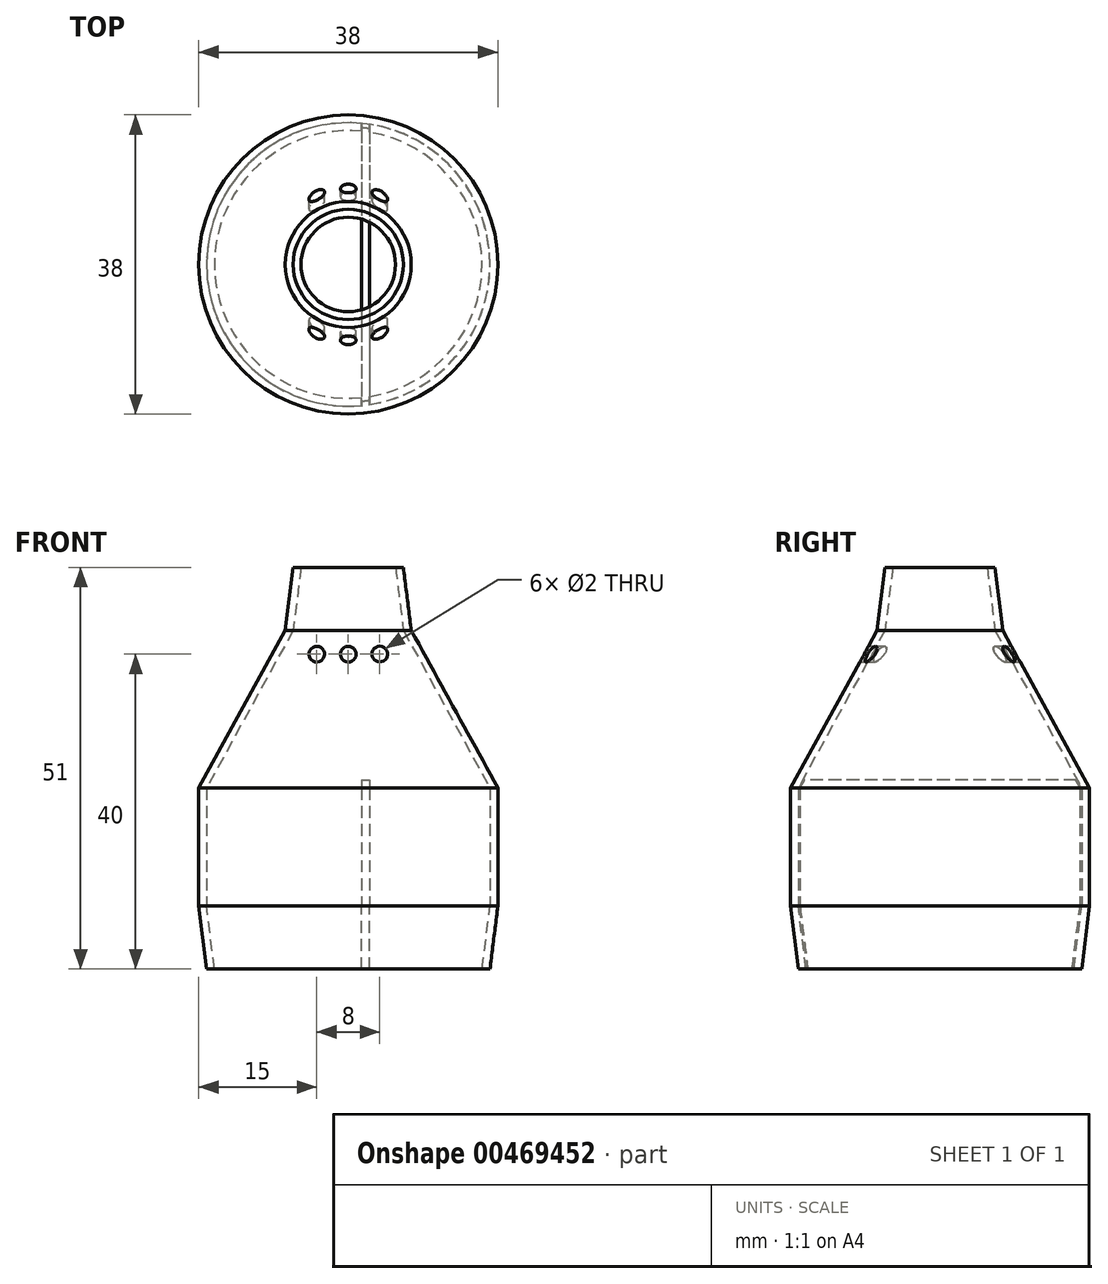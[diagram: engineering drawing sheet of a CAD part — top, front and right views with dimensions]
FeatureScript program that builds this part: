
annotation { "Feature Type Name" : "Feature", "Feature Type Description" : "" }
export const myFeature = defineFeature(function(context is Context, id is Id, definition is map)
    precondition{}
    {
        {
            var Q0;
            Q0=qCreatedBy(makeId("Top.planeOp"),FACE);
            var sketch = newSketch(context, id + "F0", { "sketchPlane" : qUnion([Q0])});
            skCircle(sketch, "E0", {"center": v(0, 0) * mm, "radius": 18 * mm});
            skCircle(sketch, "E1", {"center": v(0, 0) * mm, "radius": 19 * mm});
            skLineSegment(sketch, "E2", {"start": v(0, -19) * mm, "end": v(0, -18) * mm});
            skLineSegment(sketch, "E3.trimOffspring", {"start": v(0, 18) * mm, "end": v(0, 19) * mm});
            skPoint(sketch, "E4.center.orphan", {"position": v(-51.97, 0) * mm});
            skSolve(sketch);
        }
        {
            var Q0;
            {var subQ5=sQuery(id+"F0.wireOp",EDGE,"E2");Q0=makeQuery(id+"F0.imprint","IMPRINT",FACE,{"disambiguationData":[TD([[makeQuery(id+"F0.imprint","IMPRINT",EDGE,{"derivedFrom":subQ5}),-1.0]])]});}
            var Q1;
            {var subQ0=sQuery(id+"F0.wireOp",EDGE,"E2");Q1=makeQuery(id+"F0.imprint","IMPRINT",FACE,{"disambiguationData":[TD([[makeQuery(id+"F0.imprint","IMPRINT",EDGE,{"derivedFrom":subQ0}),1.0]])]});}
            extrude(context, id + "F1", {"entities" : qUnion([Q0, Q1]), "depth" : 15 * mm});
        }
        {
            var Q0;
            Q0=makeQuery(id+"F1.opExtrude","CAP_FACE",FACE,{"disambiguationData":[OSD([sQuery(id+"F0.wireOp",EDGE,"E0"),sQuery(id+"F0.wireOp",EDGE,"E1")])],"isStart":false});
            cPlane(context, id + "F2", {"entities" : qUnion([Q0]), "cplaneType" : CPlaneType.OFFSET, "offset" : 20 * mm, "width" : 150 * mm, "height" : 150 * mm});
        }
        {
            var Q0;
            Q0=makeQuery(id+"F1.opExtrude","CAP_FACE",FACE,{"disambiguationData":[OSD([sQuery(id+"F0.wireOp",EDGE,"E0"),sQuery(id+"F0.wireOp",EDGE,"E1")])],"isStart":false});
            var sketch = newSketch(context, id + "F3", { "sketchPlane" : qUnion([Q0])});
            skLineSegment(sketch, "E5", {"start": v(0, 19) * mm, "end": v(0, -19) * mm});
            skCircle(sketch, "E6", {"center": v(0, 0) * mm, "radius": 18 * mm});
            skCircle(sketch, "E7", {"center": v(0, 0) * mm, "radius": 19 * mm});
            skSolve(sketch);
        }
        {
            var Q0;
            Q0=qCreatedBy(id+"F2.planeOp",FACE);
            var sketch = newSketch(context, id + "F4", { "sketchPlane" : qUnion([Q0])});
            skCircle(sketch, "E8", {"center": v(0, 0) * mm, "radius": 7 * mm});
            skCircle(sketch, "E9", {"center": v(0, 0) * mm, "radius": 8 * mm});
            skLineSegment(sketch, "E10", {"start": v(0, 8) * mm, "end": v(0, 7) * mm});
            skLineSegment(sketch, "E11.trimOffspring", {"start": v(0, -7) * mm, "end": v(0, -8) * mm});
            skSolve(sketch);
        }
        {
            var Q1;
            {var subQ0=sQuery(id+"F3.wireOp",EDGE,"E7");var subQ1=sQuery(id+"F3.wireOp",EDGE,"E5");var subQ2=makeQuery(id+"F3.imprint","INTERSECT",VERTEX,{"disambiguationData":[OD(0.0)],"derivedFrom":[subQ1,subQ0]});var subQ3=sQuery(id+"F3.wireOp",EDGE,"E6");var subQ4=makeQuery(id+"F3.imprint","INTERSECT",VERTEX,{"disambiguationData":[OD(0.0)],"derivedFrom":[subQ1,subQ3]});Q1=makeQuery(id+"F3.imprint","IMPRINT",FACE,{"disambiguationData":[TD([[makeQuery(id+"F3.imprint","IMPRINT",EDGE,{"disambiguationData":[TD([[subQ2,-1.0],[subQ4,1.0]])],"derivedFrom":subQ1}),1.0]])]});}
            var Q2;
            {var subQ0=sQuery(id+"F4.wireOp",EDGE,"E10");Q2=makeQuery(id+"F4.imprint","IMPRINT",FACE,{"disambiguationData":[TD([[makeQuery(id+"F4.imprint","IMPRINT",EDGE,{"derivedFrom":subQ0}),1.0]])]});}
            loft(context, id + "F5", {"operationType" : NewBodyOperationType.ADD, "sheetProfilesArray" : [{ "sheetProfileEntities" : qUnion([Q1]) }, { "sheetProfileEntities" : qUnion([Q2]) }]});
        }
        {
            var Q1;
            {var subQ0=sQuery(id+"F3.wireOp",EDGE,"E7");var subQ1=sQuery(id+"F3.wireOp",EDGE,"E5");var subQ2=makeQuery(id+"F3.imprint","INTERSECT",VERTEX,{"disambiguationData":[OD(0.0)],"derivedFrom":[subQ1,subQ0]});var subQ3=sQuery(id+"F3.wireOp",EDGE,"E6");var subQ4=makeQuery(id+"F3.imprint","INTERSECT",VERTEX,{"disambiguationData":[OD(0.0)],"derivedFrom":[subQ1,subQ3]});Q1=makeQuery(id+"F3.imprint","IMPRINT",FACE,{"disambiguationData":[TD([[makeQuery(id+"F3.imprint","IMPRINT",EDGE,{"disambiguationData":[TD([[subQ2,-1.0],[subQ4,1.0]])],"derivedFrom":subQ1}),-1.0]])]});}
            var Q2;
            {var subQ0=sQuery(id+"F4.wireOp",EDGE,"E10");Q2=makeQuery(id+"F4.imprint","IMPRINT",FACE,{"disambiguationData":[TD([[makeQuery(id+"F4.imprint","IMPRINT",EDGE,{"derivedFrom":subQ0}),-1.0]])]});}
            loft(context, id + "F6", {"operationType" : NewBodyOperationType.ADD, "sheetProfilesArray" : [{ "sheetProfileEntities" : qUnion([Q1]) }, { "sheetProfileEntities" : qUnion([Q2]) }]});
        }
        {
            var Q0;
            Q0=qCreatedBy(makeId("Front.planeOp"),FACE);
            var sketch = newSketch(context, id + "F7", { "sketchPlane" : qUnion([Q0])});
            skCircle(sketch, "E12", {"center": v(0, 32) * mm, "radius": 1 * mm});
            skCircle(sketch, "E13", {"center": v(-4, 32) * mm, "radius": 1 * mm});
            skCircle(sketch, "E14", {"center": v(4, 32) * mm, "radius": 1 * mm});
            skLineSegment(sketch, "E15", {"start": v(-11.56, 32) * mm, "end": v(12.3, 32) * mm});
            skSolve(sketch);
        }
        {
            var Q0;
            {var subQ0=sQuery(id+"F7.wireOp",EDGE,"E15");var subQ1=sQuery(id+"F7.wireOp",EDGE,"E13");var subQ2=makeQuery(id+"F7.imprint","INTERSECT",VERTEX,{"disambiguationData":[OD(0.0)],"derivedFrom":[subQ1,subQ0]});Q0=makeQuery(id+"F7.imprint","IMPRINT",FACE,{"disambiguationData":[TD([[makeQuery(id+"F7.imprint","IMPRINT",EDGE,{"disambiguationData":[TD([[subQ2,-1.0]])],"derivedFrom":subQ1}),1.0]])]});}
            var Q1;
            {var subQ0=sQuery(id+"F7.wireOp",EDGE,"E15");var subQ1=sQuery(id+"F7.wireOp",EDGE,"E13");var subQ2=makeQuery(id+"F7.imprint","INTERSECT",VERTEX,{"disambiguationData":[OD(0.0)],"derivedFrom":[subQ1,subQ0]});Q1=makeQuery(id+"F7.imprint","IMPRINT",FACE,{"disambiguationData":[TD([[makeQuery(id+"F7.imprint","IMPRINT",EDGE,{"disambiguationData":[TD([[subQ2,1.0]])],"derivedFrom":subQ1}),1.0]])]});}
            var Q2;
            {var subQ0=sQuery(id+"F7.wireOp",EDGE,"E15");var subQ1=sQuery(id+"F7.wireOp",EDGE,"E12");var subQ2=makeQuery(id+"F7.imprint","INTERSECT",VERTEX,{"disambiguationData":[OD(0.0)],"derivedFrom":[subQ1,subQ0]});Q2=makeQuery(id+"F7.imprint","IMPRINT",FACE,{"disambiguationData":[TD([[makeQuery(id+"F7.imprint","IMPRINT",EDGE,{"disambiguationData":[TD([[subQ2,1.0]])],"derivedFrom":subQ1}),1.0]])]});}
            var Q3;
            {var subQ0=sQuery(id+"F7.wireOp",EDGE,"E15");var subQ1=sQuery(id+"F7.wireOp",EDGE,"E12");var subQ2=makeQuery(id+"F7.imprint","INTERSECT",VERTEX,{"disambiguationData":[OD(0.0)],"derivedFrom":[subQ1,subQ0]});Q3=makeQuery(id+"F7.imprint","IMPRINT",FACE,{"disambiguationData":[TD([[makeQuery(id+"F7.imprint","IMPRINT",EDGE,{"disambiguationData":[TD([[subQ2,-1.0]])],"derivedFrom":subQ1}),1.0]])]});}
            var Q4;
            {var subQ0=sQuery(id+"F7.wireOp",EDGE,"E15");var subQ1=sQuery(id+"F7.wireOp",EDGE,"E14");var subQ2=makeQuery(id+"F7.imprint","INTERSECT",VERTEX,{"disambiguationData":[OD(0.0)],"derivedFrom":[subQ1,subQ0]});Q4=makeQuery(id+"F7.imprint","IMPRINT",FACE,{"disambiguationData":[TD([[makeQuery(id+"F7.imprint","IMPRINT",EDGE,{"disambiguationData":[TD([[subQ2,1.0]])],"derivedFrom":subQ1}),1.0]])]});}
            var Q5;
            {var subQ0=sQuery(id+"F7.wireOp",EDGE,"E15");var subQ1=sQuery(id+"F7.wireOp",EDGE,"E14");var subQ2=makeQuery(id+"F7.imprint","INTERSECT",VERTEX,{"disambiguationData":[OD(0.0)],"derivedFrom":[subQ1,subQ0]});Q5=makeQuery(id+"F7.imprint","IMPRINT",FACE,{"disambiguationData":[TD([[makeQuery(id+"F7.imprint","IMPRINT",EDGE,{"disambiguationData":[TD([[subQ2,-1.0]])],"derivedFrom":subQ1}),1.0]])]});}
            extrude(context, id + "F8", {"entities" : qUnion([Q0, Q1, Q2, Q3, Q4, Q5]), "operationType" : NewBodyOperationType.REMOVE, "depth" : 12 * mm, "hasSecondDirection" : true, "secondDirectionOppositeDirection" : true, "secondDirectionDepth" : 12 * mm});
        }
        {
            var Q0;
            {var subQ0=sQuery(id+"F4.wireOp",EDGE,"E10");Q0=makeQuery(id+"F4.imprint","IMPRINT",FACE,{"disambiguationData":[TD([[makeQuery(id+"F4.imprint","IMPRINT",EDGE,{"derivedFrom":subQ0}),1.0]])]});}
            cPlane(context, id + "F9", {"entities" : qUnion([Q0]), "cplaneType" : CPlaneType.OFFSET, "offset" : 8 * mm, "width" : 150 * mm, "height" : 150 * mm});
        }
        {
            var Q0;
            Q0=qCreatedBy(id+"F9.planeOp",FACE);
            var sketch = newSketch(context, id + "F10", { "sketchPlane" : qUnion([Q0])});
            skCircle(sketch, "E16", {"center": v(0, 0) * mm, "radius": 7 * mm});
            skCircle(sketch, "E17", {"center": v(0, 0) * mm, "radius": 6 * mm});
            skLineSegment(sketch, "E18", {"start": v(0, 7) * mm, "end": v(0, 6) * mm});
            skLineSegment(sketch, "E19.trimOffspring", {"start": v(0, -6) * mm, "end": v(0, -7) * mm});
            skSolve(sketch);
        }
        {
            var Q1;
            {var subQ0=sQuery(id+"F4.wireOp",EDGE,"E10");Q1=makeQuery(id+"F4.imprint","IMPRINT",FACE,{"disambiguationData":[TD([[makeQuery(id+"F4.imprint","IMPRINT",EDGE,{"derivedFrom":subQ0}),-1.0]])]});}
            var Q2;
            {var subQ0=sQuery(id+"F10.wireOp",EDGE,"E18");Q2=makeQuery(id+"F10.imprint","IMPRINT",FACE,{"disambiguationData":[TD([[makeQuery(id+"F10.imprint","IMPRINT",EDGE,{"derivedFrom":subQ0}),-1.0]])]});}
            loft(context, id + "F11", {"operationType" : NewBodyOperationType.ADD, "sheetProfilesArray" : [{ "sheetProfileEntities" : qUnion([Q1]) }, { "sheetProfileEntities" : qUnion([Q2]) }]});
        }
        {
            var Q1;
            {var subQ0=sQuery(id+"F4.wireOp",EDGE,"E10");Q1=makeQuery(id+"F4.imprint","IMPRINT",FACE,{"disambiguationData":[TD([[makeQuery(id+"F4.imprint","IMPRINT",EDGE,{"derivedFrom":subQ0}),1.0]])]});}
            var Q2;
            {var subQ0=sQuery(id+"F10.wireOp",EDGE,"E18");Q2=makeQuery(id+"F10.imprint","IMPRINT",FACE,{"disambiguationData":[TD([[makeQuery(id+"F10.imprint","IMPRINT",EDGE,{"derivedFrom":subQ0}),1.0]])]});}
            loft(context, id + "F12", {"operationType" : NewBodyOperationType.ADD, "sheetProfilesArray" : [{ "sheetProfileEntities" : qUnion([Q1]) }, { "sheetProfileEntities" : qUnion([Q2]) }]});
        }
        {
            var Q0;
            Q0=qCreatedBy(makeId("Top.planeOp"),FACE);
            cPlane(context, id + "F13", {"entities" : qUnion([Q0]), "cplaneType" : CPlaneType.OFFSET, "offset" : 8 * mm, "oppositeDirection" : true, "width" : 150 * mm, "height" : 150 * mm});
        }
        {
            var Q0;
            Q0=qCreatedBy(id+"F13.planeOp",FACE);
            var sketch = newSketch(context, id + "F14", { "sketchPlane" : qUnion([Q0])});
            skCircle(sketch, "E20", {"center": v(0, 0) * mm, "radius": 17 * mm});
            skCircle(sketch, "E21", {"center": v(0, 0) * mm, "radius": 18 * mm});
            skLineSegment(sketch, "E22", {"start": v(0, -18) * mm, "end": v(0, 18) * mm});
            skSolve(sketch);
        }
        {
            var Q1;
            {var subQ0=sQuery(id+"F0.wireOp",EDGE,"E2");Q1=makeQuery(id+"F0.imprint","IMPRINT",FACE,{"disambiguationData":[TD([[makeQuery(id+"F0.imprint","IMPRINT",EDGE,{"derivedFrom":subQ0}),1.0]])]});}
            var Q2;
            {var subQ0=sQuery(id+"F14.wireOp",EDGE,"E22");var subQ1=sQuery(id+"F14.wireOp",EDGE,"E20");var subQ2=makeQuery(id+"F14.imprint","INTERSECT",VERTEX,{"disambiguationData":[OD(0.0)],"derivedFrom":[subQ1,subQ0]});Q2=makeQuery(id+"F14.imprint","IMPRINT",FACE,{"disambiguationData":[TD([[makeQuery(id+"F14.imprint","IMPRINT",EDGE,{"disambiguationData":[TD([[subQ2,1.0]])],"derivedFrom":subQ1}),-1.0]])]});}
            loft(context, id + "F15", {"operationType" : NewBodyOperationType.ADD, "sheetProfilesArray" : [{ "sheetProfileEntities" : qUnion([Q1]) }, { "sheetProfileEntities" : qUnion([Q2]) }]});
        }
        {
            var Q1;
            {var subQ0=sQuery(id+"F14.wireOp",EDGE,"E22");var subQ1=sQuery(id+"F14.wireOp",EDGE,"E20");var subQ2=makeQuery(id+"F14.imprint","INTERSECT",VERTEX,{"disambiguationData":[OD(0.0)],"derivedFrom":[subQ1,subQ0]});Q1=makeQuery(id+"F14.imprint","IMPRINT",FACE,{"disambiguationData":[TD([[makeQuery(id+"F14.imprint","IMPRINT",EDGE,{"disambiguationData":[TD([[subQ2,-1.0]])],"derivedFrom":subQ1}),-1.0]])]});}
            var Q2;
            {var subQ5=sQuery(id+"F0.wireOp",EDGE,"E2");Q2=makeQuery(id+"F0.imprint","IMPRINT",FACE,{"disambiguationData":[TD([[makeQuery(id+"F0.imprint","IMPRINT",EDGE,{"derivedFrom":subQ5}),-1.0]])]});}
            loft(context, id + "F16", {"operationType" : NewBodyOperationType.ADD, "sheetProfilesArray" : [{ "sheetProfileEntities" : qUnion([Q1]) }, { "sheetProfileEntities" : qUnion([Q2]) }]});
        }
        {
            var Q0;
            Q0=qCreatedBy(makeId("Top.planeOp"),FACE);
            var sketch = newSketch(context, id + "F17", { "sketchPlane" : qUnion([Q0])});
            skCircle(sketch, "E23", {"center": v(0, 0) * mm, "radius": 18 * mm});
            skLineSegment(sketch, "E24", {"start": v(1.7, 17.92) * mm, "end": v(1.7, -17.92) * mm});
            skLineSegment(sketch, "E25", {"start": v(2.7, 17.8) * mm, "end": v(2.7, -17.8) * mm});
            skSolve(sketch);
        }
        {
            var Q0;
            {var subQ0=sQuery(id+"F17.wireOp",EDGE,"E24");Q0=makeQuery(id+"F17.imprint","IMPRINT",FACE,{"disambiguationData":[TD([[makeQuery(id+"F17.imprint","IMPRINT",EDGE,{"derivedFrom":subQ0}),1.0]])]});}
            var Q1;
            Q1=makeQuery(id+"F1.opExtrude","SWEPT_BODY",BODY,{"disambiguationData":[OSD([sQuery(id+"F0.wireOp",EDGE,"E0"),sQuery(id+"F0.wireOp",EDGE,"E1")])]});
            extrude(context, id + "F18", {"entities" : qUnion([Q0]), "operationType" : NewBodyOperationType.ADD, "depth" : 16 * mm, "hasSecondDirection" : true, "secondDirectionOppositeDirection" : true, "secondDirectionBoundEntityBody" : qUnion([Q1]), "secondDirectionDepth" : 8 * mm});
        }
    });
